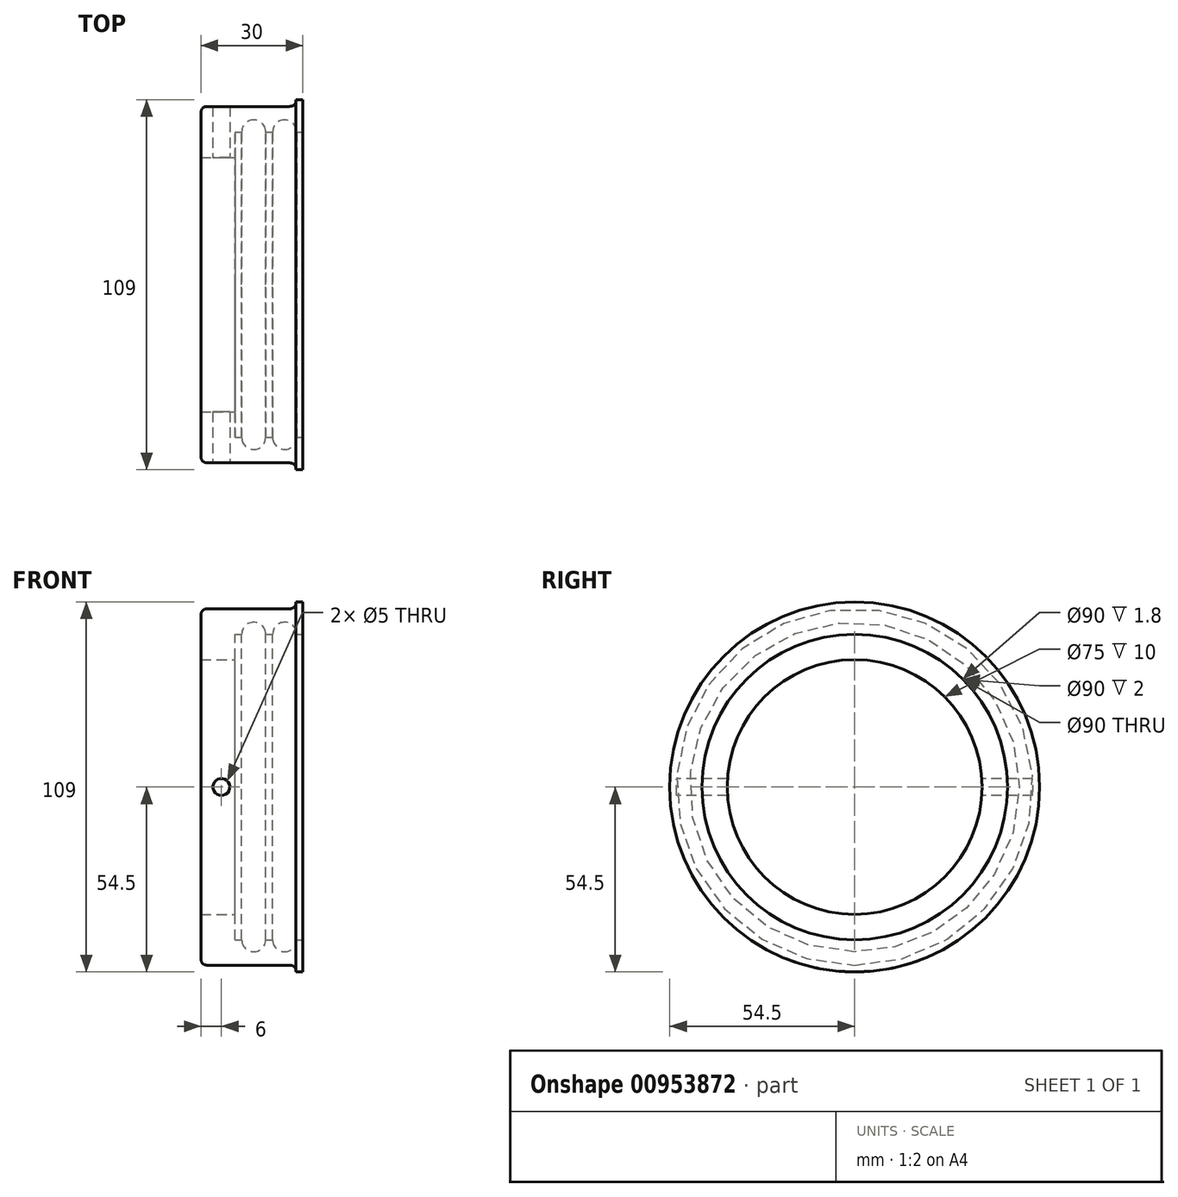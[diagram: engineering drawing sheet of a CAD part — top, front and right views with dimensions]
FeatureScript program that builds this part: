
annotation { "Feature Type Name" : "Feature", "Feature Type Description" : "" }
export const myFeature = defineFeature(function(context is Context, id is Id, definition is map)
    precondition{}
    {
        {
            var Q0;
            Q0=qCreatedBy(makeId("Front.planeOp"),FACE);
            var sketch = newSketch(context, id + "F0", { "sketchPlane" : qUnion([Q0])});
            skLineSegment(sketch, "E0", {"start": v(0, 0) * mm, "end": v(-63.65, 0) * mm, "construction": true});
            skLineSegment(sketch, "E1", {"start": v(0, 54.5) * mm, "end": v(-2, 54.5) * mm});
            skLineSegment(sketch, "E2", {"start": v(-2, 54.5) * mm, "end": v(-2, 52.5) * mm});
            skLineSegment(sketch, "E3", {"start": v(-2, 52.5) * mm, "end": v(-30, 52.5) * mm});
            skLineSegment(sketch, "E4", {"start": v(-30, 52.5) * mm, "end": v(-30, 37.5) * mm});
            skLineSegment(sketch, "E5", {"start": v(-30, 37.5) * mm, "end": v(-20, 37.5) * mm});
            skLineSegment(sketch, "E6", {"start": v(-20, 37.5) * mm, "end": v(-20, 45) * mm});
            skLineSegment(sketch, "E7", {"start": v(-20, 45) * mm, "end": v(0, 45) * mm});
            skLineSegment(sketch, "E8", {"start": v(0, 45) * mm, "end": v(0, 54.5) * mm});
            skArc(sketch, "E9", {"start": v(-10.9, 45) * mm, "mid": v(-14.45, 48.55) * mm, "end": v(-18, 45) * mm});
            skArc(sketch, "E10", {"start": v(-1.8, 45) * mm, "mid": v(-5.35, 48.55) * mm, "end": v(-8.9, 45) * mm});
            skSolve(sketch);
        }
        {
            var Q0;
            Q0=makeQuery(id+"F0.imprint","IMPRINT",FACE,{"disambiguationData":[TD([[makeQuery(id+"F0.imprint","IMPRINT",EDGE,{"derivedFrom":sQuery(id+"F0.wireOp",EDGE,"E1")}),1.0]])]});
            var Q1;
            Q1=sQuery(id+"F0.wireOp",EDGE,"E0");
            revolve(context, id + "F1", {"surfaceOperationType" : NewSurfaceOperationType.NEW, "entities" : qUnion([Q0]), "axis" : qUnion([Q1]), "revolveType" : RevolveType.FULL});
        }
        {
            var Q0;
            Q0=makeQuery(id+"F1.opRevolve","SWEPT_EDGE",EDGE,{"disambiguationData":[OSD([sQuery(id+"F0.wireOp",EDGE,"E3"),sQuery(id+"F0.wireOp",EDGE,"E4")])]});
            var Q1;
            Q1=makeQuery(id+"F1.opRevolve","SWEPT_FACE",FACE,{"disambiguationData":[OSD([sQuery(id+"F0.wireOp",EDGE,"E3")])]});
            fillet(context, id + "F2", {"entities" : qUnion([Q0, Q1]), "radius" : 2 * mm, "tangentPropagation" : true, "rho" : 0.5, "crossSection" : FilletCrossSection.CONIC, "allowEdgeOverflow" : false});
        }
        {
            var Q0;
            Q0=qCreatedBy(makeId("Front.planeOp"),FACE);
            var sketch = newSketch(context, id + "F3", { "sketchPlane" : qUnion([Q0])});
            skCircle(sketch, "E11", {"center": v(-24, 0) * mm, "radius": 2.5 * mm});
            skSolve(sketch);
        }
        {
            var Q0;
            Q0=makeQuery(id+"F3.imprint","IMPRINT",FACE,{"disambiguationData":[TD([[makeQuery(id+"F3.imprint","IMPRINT",EDGE,{"derivedFrom":sQuery(id+"F3.wireOp",EDGE,"E11")}),1.0]])]});
            var Q1;
            Q1=sQuery(id+"F3.wireOp",EDGE,"E11");
            extrude(context, id + "F4", {"entities" : qUnion([Q0]), "operationType" : NewBodyOperationType.REMOVE, "surfaceEntities" : qUnion([Q1]), "oppositeDirection" : true, "depth" : 59.92 * mm, "offsetDistance" : 25 * mm, "hasSecondDirection" : true, "secondDirectionOppositeDirection" : false, "secondDirectionDepth" : 60.98 * mm});
        }
    });
